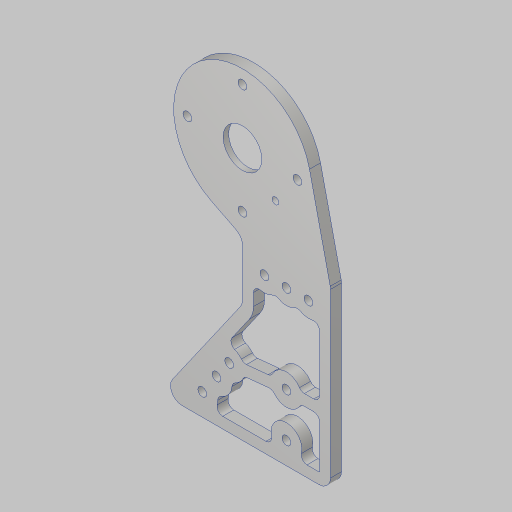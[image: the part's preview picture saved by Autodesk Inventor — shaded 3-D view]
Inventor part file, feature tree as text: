
AUTODESK INVENTOR PART (.ipt)
format: ipt  version: 2023.5 (Build 275446000, 446)  size: 362,496 bytes
history: native  units: in
note: dims shown in document units (in); Inventor stores cm internally (conversion verified against a paired STEP export)
features: sketch x6, hole x4, extrude x3, projected_geometry x3, fillet x2
ambient origin geometry x8: Origin, YZ Plane, XZ Plane, XY Plane, X Axis, Y Axis, Z Axis, Center Point
bodies: Solid1 (feature_tree)
feature tree (18):
  sketch  "Sketch1"  dims[d0=2.0in d1=15.25in]
  sketch  "Sketch2"  dims[d2=1.0in d3=17.0in d5=0.3779in]
  extrude  "Extrusion1"  Depth=15.25in
  hole  "Hole1"  [1 undecoded]
  fillet  "Fillet1"  Radius=0.3779in
  sketch  "Sketch3"  dims[d6=0.88in d7=1.875in]
  extrude  "Extrusion2"  Depth=1.875in
  hole  "Hole2"  [1 undecoded]
  hole  "Hole3"  [1 undecoded]
  extrude  "Extrusion3"  Depth=0.25in
  fillet  "Fillet2"  Radius=0.5655in
  hole  "Hole4"  [1 undecoded]
  projected_geometry  "Projected Loop1"
  sketch  "Sketch4"  dims[d8=0.625in d11=17.0in]
  sketch  "Sketch5"  dims[d12=4.0in d13=1.0in]
  projected_geometry  "Projected Loop2"
  sketch  "Sketch6"  dims[d14=0.5in d15=0.5in d16=0.5655in d17=0.5in d18=0.25in d19=0.0in d20=0.201in d21=0.75in d22=0.385in d23=0.25in d24=0.5635in d25=1.0in d26=0.8108in d27=0.26in d28=1.875in d29=2.5in d30=1.5748in d32=360.0deg d34=0.125in d35=0.0in d36=0.201in d37=0.38in d38=0.385in d39=0.25in d40=0.5635in d41=1.0in d42=0.8108in d43=1.0in d44=0.5in d45=0.201in d46=0.38in d47=0.385in d48=0.25in d49=0.5635in d50=1.0in d51=0.8108in d52=2.0in d53=0.25in d54=0.25in d55=0.125in d56=0.0in d57=0.0in d60=0.125in d61=0.125in d62=0.13in d63=1.0in d64=0.75in d65=0.156in d66=0.38in d67=0.385in d68=0.25in d69=0.5635in d70=1.0in d71=0.8108in]
  projected_geometry  "Projected Loop3"
note: 4 required parameter values undecoded (feature->parameter linkage not recoverable at this tier; creation-order binding heuristic only, values carry confidence <= 0.55)
